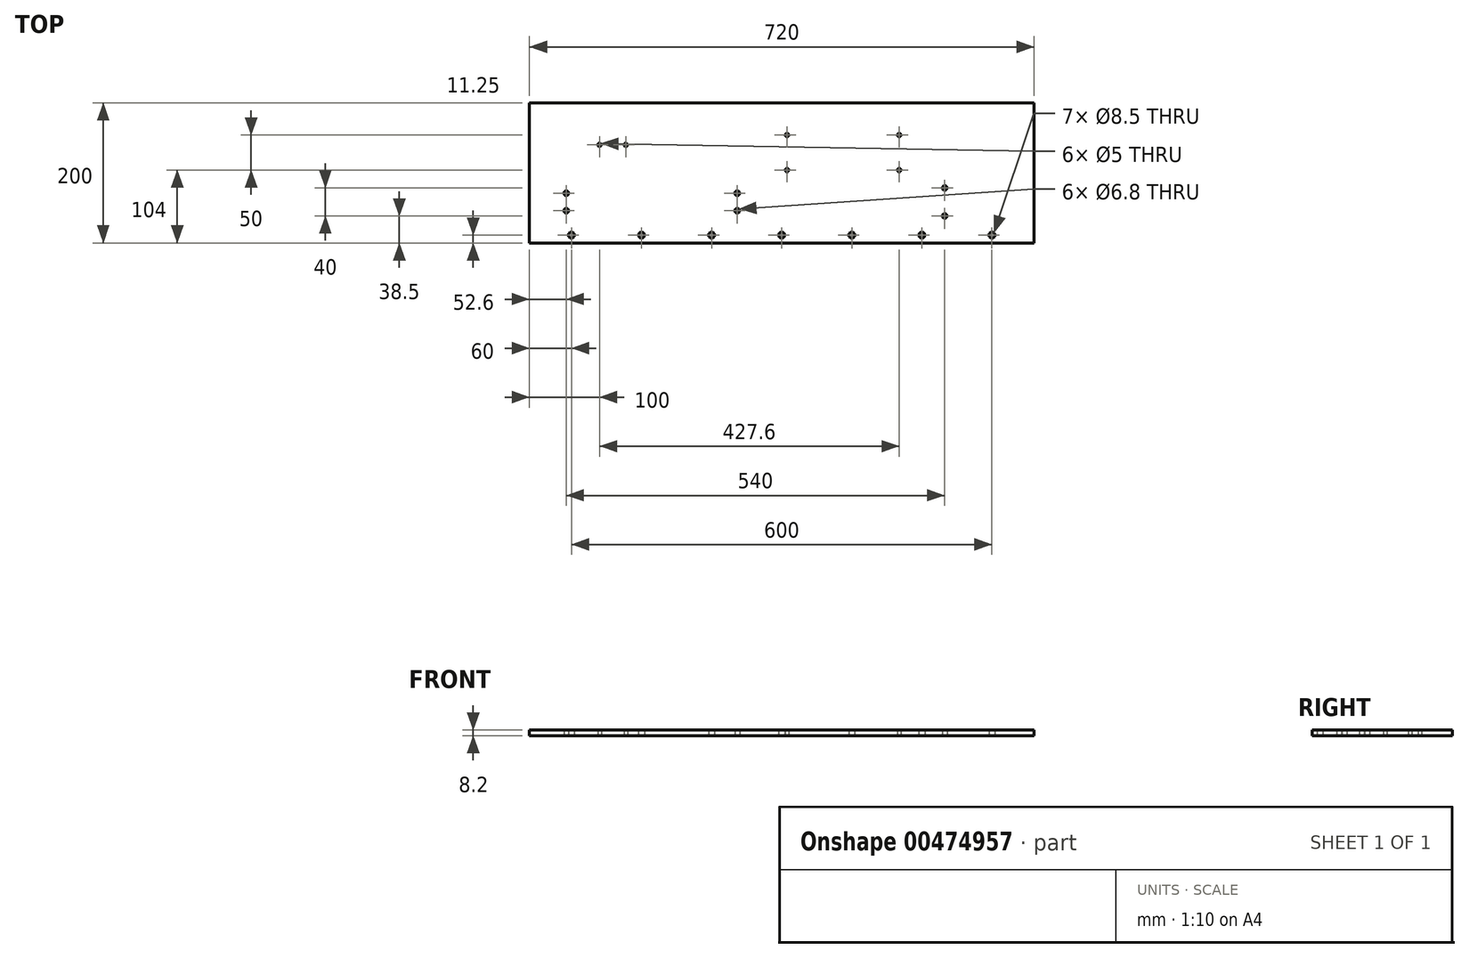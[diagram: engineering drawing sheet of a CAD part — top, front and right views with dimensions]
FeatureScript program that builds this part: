
annotation { "Feature Type Name" : "Feature", "Feature Type Description" : "" }
export const myFeature = defineFeature(function(context is Context, id is Id, definition is map)
    precondition{}
    {
        {
            var Q0;
            Q0=qCreatedBy(makeId("Top.planeOp"),FACE);
            var sketch = newSketch(context, id + "F0", { "sketchPlane" : qUnion([Q0])});
            skLineSegment(sketch, "E0.bottom", {"start": v(0, 0) * mm, "end": v(720, 0) * mm});
            skLineSegment(sketch, "E0.top", {"start": v(0, 200) * mm, "end": v(720, 200) * mm});
            skLineSegment(sketch, "E0.left", {"start": v(0, 0) * mm, "end": v(0, 200) * mm});
            skLineSegment(sketch, "E0.right", {"start": v(720, 0) * mm, "end": v(720, 200) * mm});
            skLineSegment(sketch, "E1", {"start": v(52.6, 200) * mm, "end": v(52.6, 0) * mm, "construction": true});
            skLineSegment(sketch, "E2", {"start": v(296.6, 200) * mm, "end": v(296.6, 0) * mm, "construction": true});
            skCircle(sketch, "E3", {"center": v(52.6, 71) * mm, "radius": 3.4 * mm});
            skCircle(sketch, "E4", {"center": v(52.6, 46) * mm, "radius": 3.4 * mm});
            skLineSegment(sketch, "E5", {"start": v(52.6, 200) * mm, "end": v(296.6, 200) * mm, "construction": true});
            skLineSegment(sketch, "E6", {"start": v(174.6, 200) * mm, "end": v(174.6, 0) * mm, "construction": true});
            skCircle(sketch, "E7.MirrorC", {"center": v(296.6, 46) * mm, "radius": 3.4 * mm});
            skCircle(sketch, "E8.MirrorC", {"center": v(296.6, 71) * mm, "radius": 3.4 * mm});
            skLineSegment(sketch, "E9", {"start": v(0, 11.25) * mm, "end": v(720, 11.25) * mm, "construction": true});
            skLineSegment(sketch, "E10", {"start": v(0, 58.5) * mm, "end": v(720, 58.5) * mm, "construction": true});
            skLineSegment(sketch, "E11", {"start": v(592.6, 200) * mm, "end": v(592.6, 0) * mm, "construction": true});
            skCircle(sketch, "E12", {"center": v(592.6, 78.5) * mm, "radius": 3.4 * mm});
            skCircle(sketch, "E13", {"center": v(592.6, 38.5) * mm, "radius": 3.4 * mm});
            skLineSegment(sketch, "E14", {"start": v(527.6, 200) * mm, "end": v(527.6, 0) * mm, "construction": true});
            skLineSegment(sketch, "E15", {"start": v(367.6, 200) * mm, "end": v(367.6, 0) * mm, "construction": true});
            skLineSegment(sketch, "E16", {"start": v(367.6, 129) * mm, "end": v(527.6, 129) * mm, "construction": true});
            skCircle(sketch, "E17", {"center": v(367.6, 154) * mm, "radius": 2.5 * mm});
            skCircle(sketch, "E18", {"center": v(367.6, 104) * mm, "radius": 2.5 * mm});
            skCircle(sketch, "E19", {"center": v(527.6, 154) * mm, "radius": 2.5 * mm});
            skCircle(sketch, "E20", {"center": v(527.6, 104) * mm, "radius": 2.5 * mm});
            skCircle(sketch, "E21", {"center": v(60, 11.25) * mm, "radius": 4.25 * mm});
            skCircle(sketch, "E22.1.0.0", {"center": v(160, 11.25) * mm, "radius": 4.25 * mm});
            skCircle(sketch, "E22.2.0.0", {"center": v(260, 11.25) * mm, "radius": 4.25 * mm});
            skCircle(sketch, "E22.3.0.0", {"center": v(360, 11.25) * mm, "radius": 4.25 * mm});
            skCircle(sketch, "E22.4.0.0", {"center": v(460, 11.25) * mm, "radius": 4.25 * mm});
            skCircle(sketch, "E22.5.0.0", {"center": v(560, 11.25) * mm, "radius": 4.25 * mm});
            skLineSegment(sketch, "E22.direction1", {"start": v(60, 11.25) * mm, "end": v(160, 11.25) * mm, "construction": true});
            skLineSegment(sketch, "E23", {"start": v(307.6, 200) * mm, "end": v(307.6, 0) * mm, "construction": true});
            skCircle(sketch, "E24", {"center": v(100, 140) * mm, "radius": 2.5 * mm});
            skLineSegment(sketch, "E25", {"start": v(100, 140) * mm, "end": v(174.6, 140) * mm, "construction": true});
            skCircle(sketch, "E26", {"center": v(137.5, 140) * mm, "radius": 2.5 * mm});
            skCircle(sketch, "E27.0.6.0", {"center": v(660, 11.25) * mm, "radius": 4.25 * mm});
            skSolve(sketch);
        }
        {
            var Q0;
            Q0=makeQuery(id+"F0.imprint","IMPRINT",FACE,{"disambiguationData":[TD([[makeQuery(id+"F0.imprint","IMPRINT",EDGE,{"derivedFrom":sQuery(id+"F0.wireOp",EDGE,"E0.bottom")}),1.0]])]});
            extrude(context, id + "F1", {"entities" : qUnion([Q0]), "depth" : 8.2 * mm});
        }
    });
